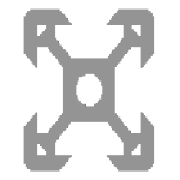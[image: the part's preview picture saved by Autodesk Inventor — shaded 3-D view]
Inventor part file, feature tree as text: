
AUTODESK INVENTOR PART (.ipt)
format: ipt  version: 2017.3 (Build 213256000, 256)  size: 195,584 bytes
history: native  units: mm
features: other x3, sketch x3, plane x1
ambient origin geometry x8: Origin, YZ Plane, XZ Plane, XY Plane, X Axis, Y Axis, Z Axis, Center Point
bodies: Solid1 (feature_tree), Body (feature_tree)
feature tree (7):
  other  "Driven Length"
  other  "Start Plane"
  other  "End Plane"
  sketch  "Sketch1"  dims[d2=4.2mm]
  sketch  "Sketch4"  dims[d3=1.5mm]
  plane  "Work Plane4"
  sketch  "Sketch5"  dims[d4=1.64mm d5=1.8mm d6=5.68mm d7=1.8mm d9=1.5mm d12=-0.0mm d13=340.0mm d14=0.13mm d15=0.0mm d18=90.0deg d17=340.0mm]
